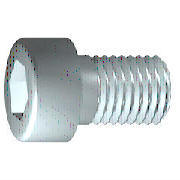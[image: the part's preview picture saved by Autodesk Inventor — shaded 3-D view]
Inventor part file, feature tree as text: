
AUTODESK INVENTOR PART (.ipt)
format: ipt  version: 2024.2 (Build 282272000, 272)  size: 200,704 bytes
history: native  units: mm (DEFAULTED — no unit token found)
features: extrude x1, plane x1, fillet x1
ambient origin geometry x7: Origin, YZ Plane, XY Plane, X Axis, Y Axis, Z Axis, Center Point
bodies: Solid1 (feature_tree), Body (feature_tree)
feature tree (3):
  extrude  "Slot"  Depth=4.875mm
  plane  "Work Plane1"
  fillet  "Fillet2"  Radius=0.276153mm
